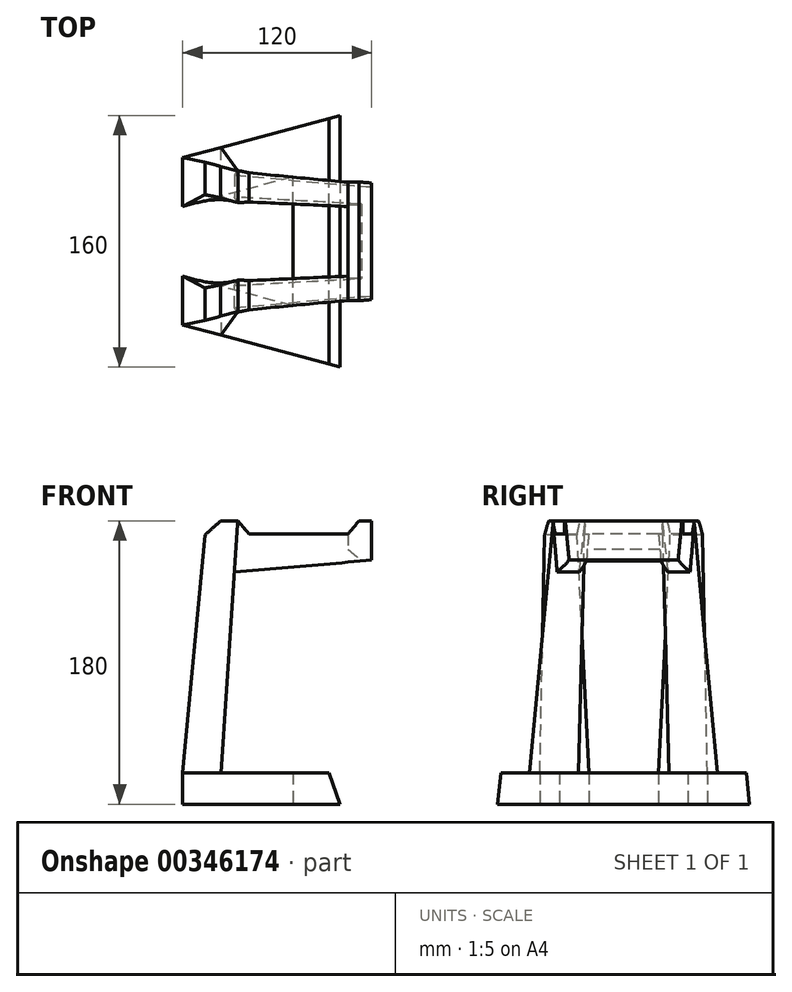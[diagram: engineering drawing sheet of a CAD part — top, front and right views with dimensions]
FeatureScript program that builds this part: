
annotation { "Feature Type Name" : "Feature", "Feature Type Description" : "" }
export const myFeature = defineFeature(function(context is Context, id is Id, definition is map)
    precondition{}
    {
        {
            var Q0;
            Q0=qCreatedBy(makeId("Top.planeOp"),FACE);
            var sketch = newSketch(context, id + "F0", { "sketchPlane" : qUnion([Q0])});
            skLineSegment(sketch, "E0", {"start": v(70, 0) * mm, "end": v(70, 40.9) * mm});
            skLineSegment(sketch, "E1", {"start": v(70, 40.9) * mm, "end": v(0, 22.15) * mm});
            skLineSegment(sketch, "E2", {"start": v(0, 22.15) * mm, "end": v(0, 53.2) * mm});
            skLineSegment(sketch, "E3", {"start": v(0, 53.2) * mm, "end": v(100, 80) * mm});
            skLineSegment(sketch, "E4", {"start": v(100, 80) * mm, "end": v(100, 0) * mm});
            skLineSegment(sketch, "E5", {"start": v(100, 0) * mm, "end": v(70, 0) * mm});
            skSolve(sketch);
        }
        {
            var Q0;
            Q0 = qSketchRegion(id + "F0", true);
            extrude(context, id + "F1", {"entities" : qUnion([Q0]), "depth" : 20 * mm});
        }
        {
            var Q0;
            Q0=makeQuery(id+"F1.opExtrude","CAP_FACE",FACE,{"disambiguationData":[OSD([sQuery(id+"F0.wireOp",EDGE,"E0"),sQuery(id+"F0.wireOp",EDGE,"E1"),sQuery(id+"F0.wireOp",EDGE,"E2"),sQuery(id+"F0.wireOp",EDGE,"E3"),sQuery(id+"F0.wireOp",EDGE,"E4"),sQuery(id+"F0.wireOp",EDGE,"E5")])],"isStart":false});
            var sketch = newSketch(context, id + "F2", { "sketchPlane" : qUnion([Q0])});
            skLineSegment(sketch, "E6", {"start": v(0, 22.15) * mm, "end": v(24.15, 28.62) * mm});
            skLineSegment(sketch, "E7", {"start": v(24.15, 28.62) * mm, "end": v(24.15, 59.68) * mm});
            skLineSegment(sketch, "E8", {"start": v(24.15, 59.68) * mm, "end": v(0, 53.2) * mm});
            skLineSegment(sketch, "E9", {"start": v(0, 53.2) * mm, "end": v(0, 22.15) * mm});
            skSolve(sketch);
        }
        {
            var Q0;
            Q0=qCreatedBy(makeId("Top.planeOp"),FACE);
            cPlane(context, id + "F3", {"entities" : qUnion([Q0]), "cplaneType" : CPlaneType.OFFSET, "offset" : 180 * mm, "width" : 150 * mm, "height" : 150 * mm});
        }
        {
            var Q0;
            Q0=qCreatedBy(id+"F3.planeOp",FACE);
            var sketch = newSketch(context, id + "F4", { "sketchPlane" : qUnion([Q0])});
            skLineSegment(sketch, "E10", {"start": v(15, 30) * mm, "end": v(35, 24.64) * mm});
            skLineSegment(sketch, "E11", {"start": v(35, 24.64) * mm, "end": v(35, 44.64) * mm});
            skLineSegment(sketch, "E12", {"start": v(35, 44.64) * mm, "end": v(15, 50) * mm});
            skLineSegment(sketch, "E13", {"start": v(15, 50) * mm, "end": v(15, 30) * mm});
            skSolve(sketch);
        }
        {
            var Q1;
            Q1=makeQuery(id+"F2.imprint","IMPRINT",FACE,{"disambiguationData":[TD([[makeQuery(id+"F2.imprint","IMPRINT",EDGE,{"derivedFrom":sQuery(id+"F2.wireOp",EDGE,"E6")}),-1.0]])]});
            var Q2;
            Q2=makeQuery(id+"F4.imprint","IMPRINT",FACE,{"disambiguationData":[TD([[makeQuery(id+"F4.imprint","IMPRINT",EDGE,{"derivedFrom":sQuery(id+"F4.wireOp",EDGE,"E10")}),1.0]])]});
            loft(context, id + "F5", {"operationType" : NewBodyOperationType.ADD, "sheetProfilesArray" : [{ "sheetProfileEntities" : qUnion([Q1]) }, { "sheetProfileEntities" : qUnion([Q2]) }]});
        }
        {
            var Q0;
            Q0=qCreatedBy(makeId("Right.planeOp"),FACE);
            cPlane(context, id + "F6", {"entities" : qUnion([Q0]), "cplaneType" : CPlaneType.OFFSET, "offset" : 120 * mm, "width" : 150 * mm, "height" : 150 * mm});
        }
        {
            var Q0;
            Q0=qCreatedBy(id+"F6.planeOp",FACE);
            var sketch = newSketch(context, id + "F7", { "sketchPlane" : qUnion([Q0])});
            skLineSegment(sketch, "E14.bottom", {"start": v(37.5, 180) * mm, "end": v(20, 180) * mm});
            skLineSegment(sketch, "E14.top", {"start": v(37.5, 145) * mm, "end": v(20, 145) * mm});
            skLineSegment(sketch, "E14.left", {"start": v(37.5, 180) * mm, "end": v(37.5, 145) * mm});
            skLineSegment(sketch, "E14.right", {"start": v(20, 180) * mm, "end": v(20, 145) * mm});
            skSolve(sketch);
        }
        {
            var Q0;
            Q0=makeQuery(id+"F5.opLoft","SWEPT_FACE",FACE,{"disambiguationData":[OSD([sQuery(id+"F0.wireOp",EDGE,"E1"),sQuery(id+"F0.wireOp",EDGE,"E3"),sQuery(id+"F2.wireOp",EDGE,"E6"),sQuery(id+"F2.wireOp",EDGE,"E7"),sQuery(id+"F2.wireOp",EDGE,"E8"),sQuery(id+"F4.wireOp",EDGE,"E10"),sQuery(id+"F4.wireOp",EDGE,"E11"),sQuery(id+"F4.wireOp",EDGE,"E12")])]});
            var sketch = newSketch(context, id + "F8", { "sketchPlane" : qUnion([Q0])});
            skLineSegment(sketch, "E15", {"start": v(24.64, 181.96) * mm, "end": v(44.64, 181.96) * mm});
            skLineSegment(sketch, "E16", {"start": v(44.64, 181.96) * mm, "end": v(47.92, 146.96) * mm});
            skLineSegment(sketch, "E17", {"start": v(47.92, 146.96) * mm, "end": v(25.5, 146.96) * mm});
            skLineSegment(sketch, "E18", {"start": v(25.5, 146.96) * mm, "end": v(24.64, 181.96) * mm});
            skSolve(sketch);
        }
        {
            var Q1;
            Q1=makeQuery(id+"F8.imprint","IMPRINT",FACE,{"disambiguationData":[TD([[makeQuery(id+"F8.imprint","IMPRINT",EDGE,{"derivedFrom":sQuery(id+"F8.wireOp",EDGE,"E15")}),-1.0]])]});
            var Q2;
            Q2=makeQuery(id+"F7.imprint","IMPRINT",FACE,{"disambiguationData":[TD([[makeQuery(id+"F7.imprint","IMPRINT",EDGE,{"derivedFrom":sQuery(id+"F7.wireOp",EDGE,"E14.bottom")}),1.0]])]});
            loft(context, id + "F9", {"operationType" : NewBodyOperationType.ADD, "sheetProfilesArray" : [{ "sheetProfileEntities" : qUnion([Q1]) }, { "sheetProfileEntities" : qUnion([Q2]) }]});
        }
        {
            var Q0;
            Q0=qCreatedBy(makeId("Front.planeOp"),FACE);
            var sketch = newSketch(context, id + "F10", { "sketchPlane" : qUnion([Q0])});
            skLineSegment(sketch, "E19", {"start": v(112, 180) * mm, "end": v(35, 180) * mm});
            skLineSegment(sketch, "E20", {"start": v(35, 180) * mm, "end": v(42, 171.66) * mm});
            skLineSegment(sketch, "E21", {"start": v(42, 171.66) * mm, "end": v(105, 171.66) * mm});
            skLineSegment(sketch, "E22", {"start": v(105, 171.66) * mm, "end": v(112, 180) * mm});
            skSolve(sketch);
        }
        {
            var Q0;
            Q0 = qSketchRegion(id + "F10", true);
            extrude(context, id + "F11", {"entities" : qUnion([Q0]), "operationType" : NewBodyOperationType.REMOVE, "oppositeDirection" : true, "depth" : 71 * mm});
        }
        {
            var Q0;
            Q0=makeQuery(id+"F9.opLoft","MID_CAP_EDGE",EDGE,{"disambiguationData":[OSD([sQuery(id+"F7.wireOp",EDGE,"E14.top"),sQuery(id+"F7.wireOp",EDGE,"E14.left"),sQuery(id+"F7.wireOp",EDGE,"E14.right")])],"capPos":1.0});
            chamfer(context, id + "F12", {"entities" : qUnion([Q0]), "chamferType" : ChamferType.OFFSET_ANGLE, "width" : 10 * mm, "oppositeDirection" : false, "angle" : 85 * degree, "tangentPropagation" : true});
        }
        {
            var Q0;
            {var subQ0=sQuery(id+"F7.wireOp",EDGE,"E14.right");var subQ1=sQuery(id+"F7.wireOp",EDGE,"E14.top");Q0=makeQuery(id+"F12.opChamfer","BLEND_EDGE",EDGE,{"blendedFrom":[makeQuery(id+"F9.opLoft","MID_CAP_EDGE",EDGE,{"disambiguationData":[OSD([subQ1,sQuery(id+"F7.wireOp",EDGE,"E14.left"),subQ0])],"capPos":1.0}),makeQuery(id+"F9.opLoft","SWEPT_FACE",FACE,{"disambiguationData":[OSD([sQuery(id+"F0.wireOp",EDGE,"E1"),sQuery(id+"F2.wireOp",EDGE,"E6"),sQuery(id+"F2.wireOp",EDGE,"E7"),sQuery(id+"F4.wireOp",EDGE,"E10"),sQuery(id+"F4.wireOp",EDGE,"E11"),sQuery(id+"F7.wireOp",EDGE,"E14.bottom"),subQ1,subQ0,sQuery(id+"F8.wireOp",EDGE,"E15"),sQuery(id+"F8.wireOp",EDGE,"E17"),sQuery(id+"F8.wireOp",EDGE,"E18")])]})],"blendedInto":[makeQuery(id+"F9.opLoft","SWEPT_FACE",FACE,{"disambiguationData":[OSD([sQuery(id+"F0.wireOp",EDGE,"E1"),sQuery(id+"F2.wireOp",EDGE,"E6"),sQuery(id+"F2.wireOp",EDGE,"E7"),sQuery(id+"F4.wireOp",EDGE,"E10"),sQuery(id+"F4.wireOp",EDGE,"E11"),sQuery(id+"F7.wireOp",EDGE,"E14.bottom"),subQ1,subQ0,sQuery(id+"F8.wireOp",EDGE,"E15"),sQuery(id+"F8.wireOp",EDGE,"E17"),sQuery(id+"F8.wireOp",EDGE,"E18")])]})]});}
            var Q1;
            {var subQ0=sQuery(id+"F7.wireOp",EDGE,"E14.left");var subQ1=sQuery(id+"F7.wireOp",EDGE,"E14.top");Q1=makeQuery(id+"F12.opChamfer","BLEND_EDGE",EDGE,{"blendedFrom":[makeQuery(id+"F9.opLoft","MID_CAP_EDGE",EDGE,{"disambiguationData":[OSD([subQ1,subQ0,sQuery(id+"F7.wireOp",EDGE,"E14.right")])],"capPos":1.0}),makeQuery(id+"F9.opLoft","SWEPT_FACE",FACE,{"disambiguationData":[OSD([sQuery(id+"F0.wireOp",EDGE,"E3"),sQuery(id+"F2.wireOp",EDGE,"E7"),sQuery(id+"F2.wireOp",EDGE,"E8"),sQuery(id+"F4.wireOp",EDGE,"E11"),sQuery(id+"F4.wireOp",EDGE,"E12"),sQuery(id+"F7.wireOp",EDGE,"E14.bottom"),subQ1,subQ0,sQuery(id+"F8.wireOp",EDGE,"E15"),sQuery(id+"F8.wireOp",EDGE,"E16"),sQuery(id+"F8.wireOp",EDGE,"E17")])]})],"blendedInto":[makeQuery(id+"F9.opLoft","SWEPT_FACE",FACE,{"disambiguationData":[OSD([sQuery(id+"F0.wireOp",EDGE,"E3"),sQuery(id+"F2.wireOp",EDGE,"E7"),sQuery(id+"F2.wireOp",EDGE,"E8"),sQuery(id+"F4.wireOp",EDGE,"E11"),sQuery(id+"F4.wireOp",EDGE,"E12"),sQuery(id+"F7.wireOp",EDGE,"E14.bottom"),subQ1,subQ0,sQuery(id+"F8.wireOp",EDGE,"E15"),sQuery(id+"F8.wireOp",EDGE,"E16"),sQuery(id+"F8.wireOp",EDGE,"E17")])]})]});}
            chamfer(context, id + "F13", {"entities" : qUnion([Q0, Q1]), "chamferType" : ChamferType.OFFSET_ANGLE, "width" : 30 * mm, "oppositeDirection" : false, "angle" : 5 * degree, "tangentPropagation" : true});
        }
        {
            var Q0;
            Q0=qCreatedBy(makeId("Front.planeOp"),FACE);
            var sketch = newSketch(context, id + "F14", { "sketchPlane" : qUnion([Q0])});
            skLineSegment(sketch, "E23", {"start": v(112, 180) * mm, "end": v(120, 180) * mm});
            skLineSegment(sketch, "E24", {"start": v(120, 180) * mm, "end": v(120, 155) * mm});
            skLineSegment(sketch, "E25", {"start": v(120, 155) * mm, "end": v(113.6, 154.44) * mm});
            skLineSegment(sketch, "E26", {"start": v(113.6, 154.44) * mm, "end": v(105, 161.66) * mm});
            skLineSegment(sketch, "E27", {"start": v(105, 161.66) * mm, "end": v(105, 171.66) * mm});
            skLineSegment(sketch, "E28", {"start": v(105, 171.66) * mm, "end": v(112, 180) * mm});
            skSolve(sketch);
        }
        {
            var Q0;
            Q0=makeQuery(id+"F14.imprint","IMPRINT",FACE,{"disambiguationData":[TD([[makeQuery(id+"F14.imprint","IMPRINT",EDGE,{"derivedFrom":sQuery(id+"F14.wireOp",EDGE,"E23")}),-1.0]])]});
            extrude(context, id + "F15", {"entities" : qUnion([Q0]), "operationType" : NewBodyOperationType.ADD, "endBound" : BoundingType.UP_TO_NEXT, "oppositeDirection" : true, "depth" : 25 * mm});
        }
        {
            var Q0;
            Q0=makeQuery(id+"F1.opExtrude","SWEPT_BODY",BODY,{"disambiguationData":[OSD([sQuery(id+"F0.wireOp",EDGE,"E0"),sQuery(id+"F0.wireOp",EDGE,"E1"),sQuery(id+"F0.wireOp",EDGE,"E2"),sQuery(id+"F0.wireOp",EDGE,"E3"),sQuery(id+"F0.wireOp",EDGE,"E4"),sQuery(id+"F0.wireOp",EDGE,"E5")])]});
            var Q1;
            Q1=qCreatedBy(makeId("Front.planeOp"),FACE);
            mirror(context, id + "F16", {"operationType" : NewBodyOperationType.ADD, "entities" : qUnion([Q0]), "mirrorPlane" : qUnion([Q1])});
        }
        {
            var Q0;
            {var subQ0=makeQuery(id+"F1.opExtrude","CAP_EDGE",EDGE,{"disambiguationData":[OSD([sQuery(id+"F0.wireOp",EDGE,"E4")])],"isStart":false});Q0=makeQuery(id+"F16.boolean.opBoolean","MERGE",EDGE,{"derivedFrom":[subQ0,makeQuery(id+"F16.opPattern","COPY",EDGE,{"derivedFrom":subQ0,"instanceName":"1"})]});}
            chamfer(context, id + "F17", {"entities" : qUnion([Q0]), "chamferType" : ChamferType.OFFSET_ANGLE, "width" : 20 * mm, "oppositeDirection" : false, "angle" : 20 * degree, "tangentPropagation" : true});
        }
        {
            var Q0;
            Q0=makeQuery(id+"F5.opLoft","MID_CAP_EDGE",EDGE,{"disambiguationData":[OSD([sQuery(id+"F4.wireOp",EDGE,"E10"),sQuery(id+"F4.wireOp",EDGE,"E12"),sQuery(id+"F4.wireOp",EDGE,"E13")])],"capPos":1.0});
            var Q1;
            Q1=makeQuery(id+"F16.opPattern","COPY",EDGE,{"derivedFrom":makeQuery(id+"F5.opLoft","MID_CAP_EDGE",EDGE,{"disambiguationData":[OSD([sQuery(id+"F4.wireOp",EDGE,"E10"),sQuery(id+"F4.wireOp",EDGE,"E12"),sQuery(id+"F4.wireOp",EDGE,"E13")])],"capPos":1.0}),"instanceName":"1"});
            chamfer(context, id + "F18", {"entities" : qUnion([Q0, Q1]), "width" : 10 * mm, "tangentPropagation" : true});
        }
    });
